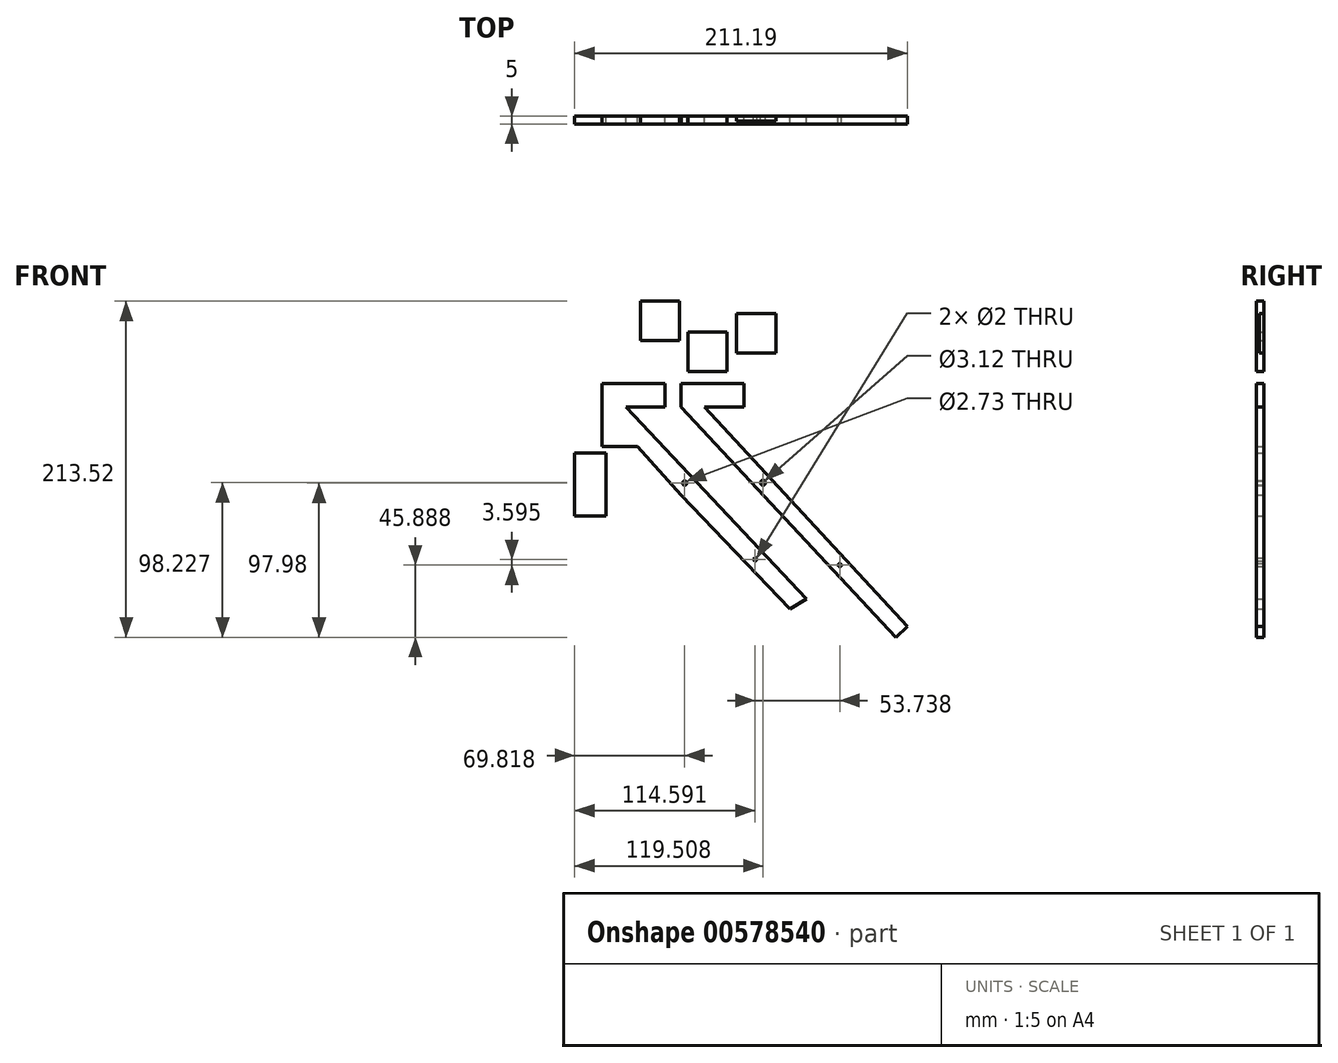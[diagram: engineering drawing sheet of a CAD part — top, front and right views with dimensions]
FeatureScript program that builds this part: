
annotation { "Feature Type Name" : "Feature", "Feature Type Description" : "" }
export const myFeature = defineFeature(function(context is Context, id is Id, definition is map)
    precondition{}
    {
        {
            var Q0;
            Q0=qCreatedBy(makeId("Front.planeOp"),FACE);
            var sketch = newSketch(context, id + "F0", { "sketchPlane" : qUnion([Q0])});
            skLineSegment(sketch, "E0", {"start": v(0, 0) * mm, "end": v(0, 15) * mm});
            skLineSegment(sketch, "E1", {"start": v(0, 15) * mm, "end": v(40, 15) * mm});
            skLineSegment(sketch, "E2", {"start": v(40, 15) * mm, "end": v(40, 0) * mm});
            skLineSegment(sketch, "E3", {"start": v(40, 0) * mm, "end": v(15, 0) * mm});
            skLineSegment(sketch, "E4", {"start": v(0, 0) * mm, "end": v(136.44, -146.24) * mm});
            skLineSegment(sketch, "E5", {"start": v(136.44, -146.24) * mm, "end": v(143.75, -139.41) * mm});
            skLineSegment(sketch, "E6", {"start": v(143.75, -139.41) * mm, "end": v(15, 0) * mm});
            skCircle(sketch, "E7", {"center": v(52.07, -48.01) * mm, "radius": 1.56 * mm});
            skCircle(sketch, "E8", {"center": v(100.89, -100.35) * mm, "radius": 1 * mm});
            skSolve(sketch);
        }
        {
            var Q0;
            Q0=qCreatedBy(makeId("Front.planeOp"),FACE);
            var sketch = newSketch(context, id + "F1", { "sketchPlane" : qUnion([Q0])});
            skLineSegment(sketch, "E9", {"start": v(0, 0) * mm, "end": v(-10, 0) * mm});
            skLineSegment(sketch, "E10", {"start": v(-10, 0) * mm, "end": v(-10, 15) * mm});
            skLineSegment(sketch, "E11", {"start": v(-10, 15) * mm, "end": v(-50, 15) * mm});
            skLineSegment(sketch, "E12", {"start": v(-50, 15) * mm, "end": v(-50, 0) * mm});
            skLineSegment(sketch, "E13", {"start": v(-10, 0) * mm, "end": v(-35, 0) * mm});
            skLineSegment(sketch, "E14", {"start": v(-50, 0) * mm, "end": v(0, -55.9) * mm});
            skLineSegment(sketch, "E15", {"start": v(79.86, -121.83) * mm, "end": v(-35, 0) * mm});
            skLineSegment(sketch, "E16", {"start": v(-50, 0) * mm, "end": v(-50, -25) * mm});
            skLineSegment(sketch, "E17", {"start": v(-50, -25) * mm, "end": v(-27.64, -25) * mm});
            skCircle(sketch, "E18", {"center": v(2.38, -48.26) * mm, "radius": 1.37 * mm});
            skLineSegment(sketch, "E19", {"start": v(69.3, -128.25) * mm, "end": v(0, -55.9) * mm});
            skLineSegment(sketch, "E20", {"start": v(79.86, -121.83) * mm, "end": v(69.3, -128.25) * mm});
            skCircle(sketch, "E21", {"center": v(47.15, -96.76) * mm, "radius": 1 * mm});
            skSolve(sketch);
        }
        {
            var Q0;
            Q0=makeQuery(id+"F1.imprint","IMPRINT",FACE,{"disambiguationData":[TD([[makeQuery(id+"F1.imprint","IMPRINT",EDGE,{"derivedFrom":sQuery(id+"F1.wireOp",EDGE,"E10")}),1.0]])]});
            var Q1;
            {var subQ0=sQuery(id+"F1.wireOp",EDGE,"E16");Q1=makeQuery(id+"F1.imprint","IMPRINT",FACE,{"disambiguationData":[TD([[makeQuery(id+"F1.imprint","IMPRINT",EDGE,{"derivedFrom":subQ0}),1.0]])]});}
            extrude(context, id + "F2", {"entities" : qUnion([Q0, Q1]), "depth" : 5 * mm, "offsetDistance" : 25 * mm});
        }
        {
            var Q0;
            Q0=makeQuery(id+"F0.imprint","IMPRINT",FACE,{"disambiguationData":[TD([[makeQuery(id+"F0.imprint","IMPRINT",EDGE,{"derivedFrom":sQuery(id+"F0.wireOp",EDGE,"E0")}),-1.0]])]});
            extrude(context, id + "F3", {"entities" : qUnion([Q0]), "depth" : 5 * mm, "offsetDistance" : 25 * mm});
        }
        {
            var Q0;
            Q0=qCreatedBy(makeId("Front.planeOp"),FACE);
            var sketch = newSketch(context, id + "F4", { "sketchPlane" : qUnion([Q0])});
            skLineSegment(sketch, "E22.bottom", {"start": v(60.36, 59.48) * mm, "end": v(35.36, 59.48) * mm});
            skLineSegment(sketch, "E22.top", {"start": v(60.36, 34.48) * mm, "end": v(35.36, 34.48) * mm});
            skLineSegment(sketch, "E22.left", {"start": v(60.36, 59.48) * mm, "end": v(60.36, 34.48) * mm});
            skLineSegment(sketch, "E22.right", {"start": v(35.36, 59.48) * mm, "end": v(35.36, 34.48) * mm});
            skSolve(sketch);
        }
        {
            var Q0;
            Q0=makeQuery(id+"F4.imprint","IMPRINT",FACE,{"disambiguationData":[TD([[makeQuery(id+"F4.imprint","IMPRINT",EDGE,{"derivedFrom":sQuery(id+"F4.wireOp",EDGE,"E22.bottom")}),1.0]])]});
            extrude(context, id + "F5", {"entities" : qUnion([Q0]), "depth" : 3 * mm, "offsetDistance" : 25 * mm});
        }
        {
            var Q0;
            Q0=qCreatedBy(makeId("Front.planeOp"),FACE);
            var sketch = newSketch(context, id + "F6", { "sketchPlane" : qUnion([Q0])});
            skLineSegment(sketch, "E23.bottom", {"start": v(-0.8, 67.28) * mm, "end": v(-25.8, 67.28) * mm});
            skLineSegment(sketch, "E23.top", {"start": v(-0.8, 42.28) * mm, "end": v(-25.8, 42.28) * mm});
            skLineSegment(sketch, "E23.left", {"start": v(-0.8, 67.28) * mm, "end": v(-0.8, 42.28) * mm});
            skLineSegment(sketch, "E23.right", {"start": v(-25.8, 67.28) * mm, "end": v(-25.8, 42.28) * mm});
            skSolve(sketch);
        }
        {
            var Q0;
            Q0=makeQuery(id+"F6.imprint","IMPRINT",FACE,{"disambiguationData":[TD([[makeQuery(id+"F6.imprint","IMPRINT",EDGE,{"derivedFrom":sQuery(id+"F6.wireOp",EDGE,"E23.bottom")}),1.0]])]});
            extrude(context, id + "F7", {"entities" : qUnion([Q0]), "depth" : 5 * mm, "offsetDistance" : 25 * mm});
        }
        {
            var Q0;
            Q0=qCreatedBy(makeId("Front.planeOp"),FACE);
            var sketch = newSketch(context, id + "F8", { "sketchPlane" : qUnion([Q0])});
            skLineSegment(sketch, "E24.bottom", {"start": v(29.38, 47.6) * mm, "end": v(4.38, 47.6) * mm});
            skLineSegment(sketch, "E24.top", {"start": v(29.38, 22.6) * mm, "end": v(4.38, 22.6) * mm});
            skLineSegment(sketch, "E24.left", {"start": v(29.38, 47.6) * mm, "end": v(29.38, 22.6) * mm});
            skLineSegment(sketch, "E24.right", {"start": v(4.38, 47.6) * mm, "end": v(4.38, 22.6) * mm});
            skSolve(sketch);
        }
        {
            var Q0;
            Q0 = qSketchRegion(id + "F8", true);
            extrude(context, id + "F9", {"entities" : qUnion([Q0]), "depth" : 5 * mm, "offsetDistance" : 25 * mm});
        }
        {
            var Q0;
            Q0=qCreatedBy(makeId("Front.planeOp"),FACE);
            var sketch = newSketch(context, id + "F10", { "sketchPlane" : qUnion([Q0])});
            skLineSegment(sketch, "E25.bottom", {"start": v(-47.44, -69.26) * mm, "end": v(-67.44, -69.26) * mm});
            skLineSegment(sketch, "E25.top", {"start": v(-47.44, -29.26) * mm, "end": v(-67.44, -29.26) * mm});
            skLineSegment(sketch, "E25.left", {"start": v(-47.44, -69.26) * mm, "end": v(-47.44, -29.26) * mm});
            skLineSegment(sketch, "E25.right", {"start": v(-67.44, -69.26) * mm, "end": v(-67.44, -29.26) * mm});
            skSolve(sketch);
        }
        {
            var Q0;
            Q0=makeQuery(id+"F10.imprint","IMPRINT",FACE,{"disambiguationData":[TD([[makeQuery(id+"F10.imprint","IMPRINT",EDGE,{"derivedFrom":sQuery(id+"F10.wireOp",EDGE,"E25.bottom")}),-1.0]])]});
            extrude(context, id + "F11", {"entities" : qUnion([Q0]), "depth" : 5 * mm, "offsetDistance" : 25 * mm});
        }
    });
